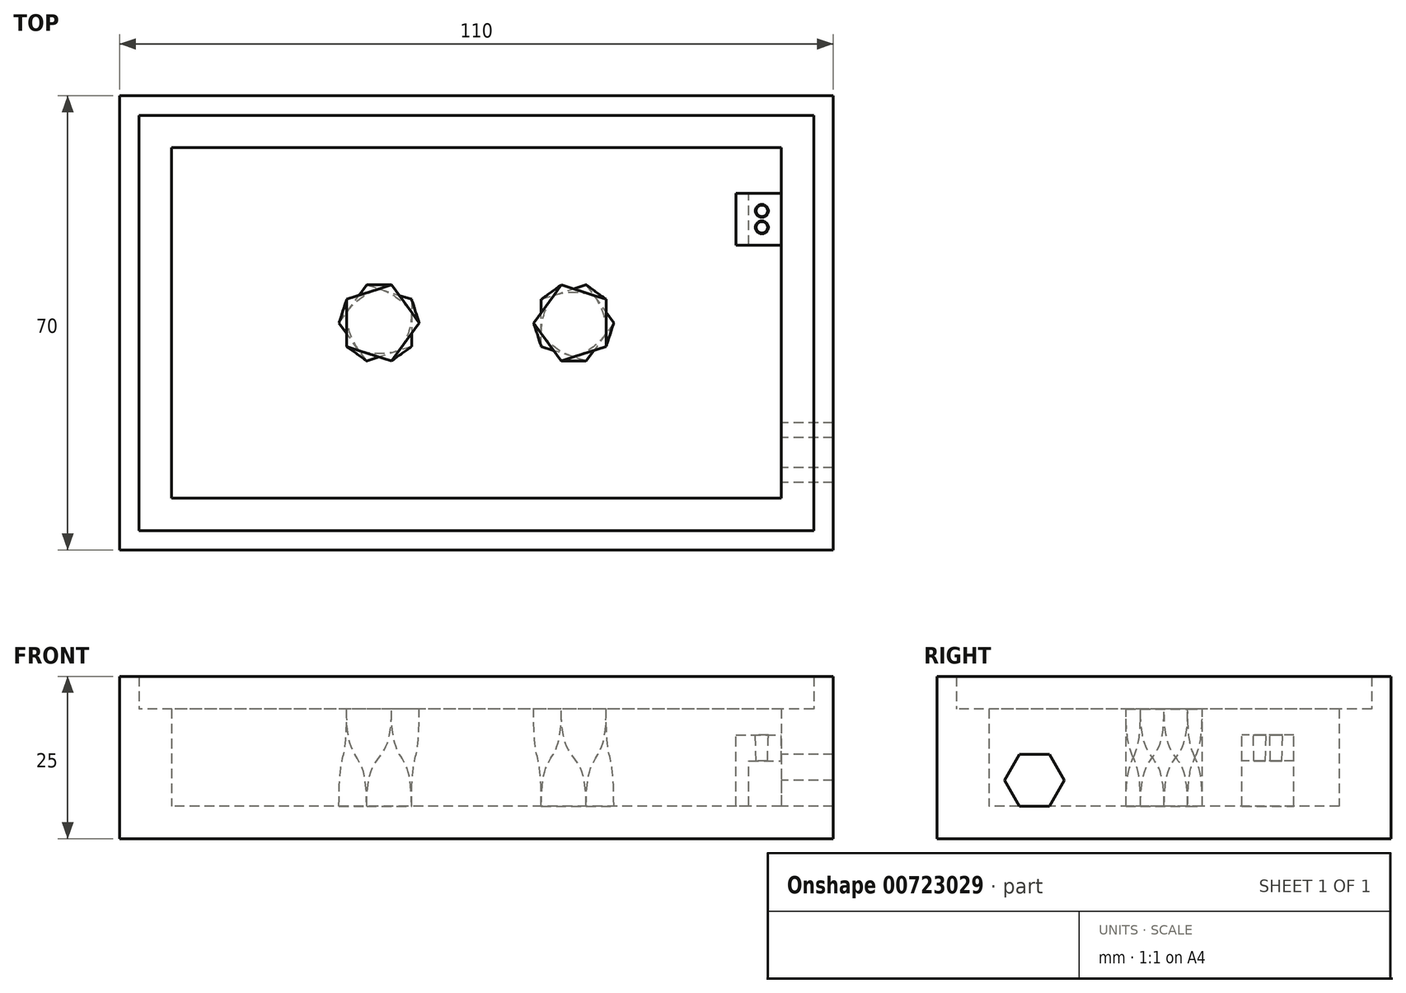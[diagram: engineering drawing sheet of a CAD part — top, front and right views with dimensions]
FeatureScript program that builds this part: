
annotation { "Feature Type Name" : "Feature", "Feature Type Description" : "" }
export const myFeature = defineFeature(function(context is Context, id is Id, definition is map)
    precondition{}
    {
        {
            var Q0;
            Q0=qCreatedBy(makeId("Top.planeOp"),FACE);
            var sketch = newSketch(context, id + "F0", { "sketchPlane" : qUnion([Q0])});
            skLineSegment(sketch, "E0.bottom", {"start": v(55, 35) * mm, "end": v(-55, 35) * mm});
            skLineSegment(sketch, "E0.top", {"start": v(55, -35) * mm, "end": v(-55, -35) * mm});
            skLineSegment(sketch, "E0.left", {"start": v(55, 35) * mm, "end": v(55, -35) * mm});
            skLineSegment(sketch, "E0.right", {"start": v(-55, 35) * mm, "end": v(-55, -35) * mm});
            skPoint(sketch, "E1", {"position": v(0, 35) * mm});
            skPoint(sketch, "E2", {"position": v(55, 0) * mm});
            skLineSegment(sketch, "E3.0", {"start": v(47, 27) * mm, "end": v(-47, 27) * mm});
            skLineSegment(sketch, "E3.1", {"start": v(47, 27) * mm, "end": v(47, -27) * mm});
            skLineSegment(sketch, "E3.2", {"start": v(47, -27) * mm, "end": v(-47, -27) * mm});
            skLineSegment(sketch, "E3.3", {"start": v(-47, 27) * mm, "end": v(-47, -27) * mm});
            skSolve(sketch);
        }
        {
            var Q0;
            Q0 = qSketchRegion(id + "F0", true);
            extrude(context, id + "F1", {"entities" : qUnion([Q0]), "depth" : 20 * mm, "offsetDistance" : 25 * mm});
        }
        {
            var Q0;
            Q0=makeQuery(id+"F1.opExtrude","CAP_FACE",FACE,{"disambiguationData":[OSD([sQuery(id+"F0.wireOp",EDGE,"E0.bottom"),sQuery(id+"F0.wireOp",EDGE,"E0.top"),sQuery(id+"F0.wireOp",EDGE,"E0.left"),sQuery(id+"F0.wireOp",EDGE,"E0.right"),sQuery(id+"F0.wireOp",EDGE,"E3.0"),sQuery(id+"F0.wireOp",EDGE,"E3.1"),sQuery(id+"F0.wireOp",EDGE,"E3.2"),sQuery(id+"F0.wireOp",EDGE,"E3.3")])],"isStart":false});
            var sketch = newSketch(context, id + "F2", { "sketchPlane" : qUnion([Q0])});
            skLineSegment(sketch, "E4.bottom", {"start": v(55, 35) * mm, "end": v(-55, 35) * mm});
            skLineSegment(sketch, "E4.top", {"start": v(55, -35) * mm, "end": v(-55, -35) * mm});
            skLineSegment(sketch, "E4.left", {"start": v(55, 35) * mm, "end": v(55, -35) * mm});
            skLineSegment(sketch, "E4.right", {"start": v(-55, 35) * mm, "end": v(-55, -35) * mm});
            skLineSegment(sketch, "E5.bottom", {"start": v(52, 32) * mm, "end": v(-52, 32) * mm});
            skLineSegment(sketch, "E5.top", {"start": v(52, -32) * mm, "end": v(-52, -32) * mm});
            skLineSegment(sketch, "E5.left", {"start": v(52, 32) * mm, "end": v(52, -32) * mm});
            skLineSegment(sketch, "E5.right", {"start": v(-52, 32) * mm, "end": v(-52, -32) * mm});
            skSolve(sketch);
        }
        {
            var Q0;
            Q0 = qSketchRegion(id + "F2", true);
            extrude(context, id + "F3", {"entities" : qUnion([Q0]), "operationType" : NewBodyOperationType.ADD, "depth" : 5 * mm, "offsetDistance" : 25 * mm});
        }
        {
            var Q0;
            Q0=makeQuery(id+"F1.opExtrude","CAP_FACE",FACE,{"disambiguationData":[OSD([sQuery(id+"F0.wireOp",EDGE,"E0.bottom"),sQuery(id+"F0.wireOp",EDGE,"E0.top"),sQuery(id+"F0.wireOp",EDGE,"E0.left"),sQuery(id+"F0.wireOp",EDGE,"E0.right"),sQuery(id+"F0.wireOp",EDGE,"E3.0"),sQuery(id+"F0.wireOp",EDGE,"E3.1"),sQuery(id+"F0.wireOp",EDGE,"E3.2"),sQuery(id+"F0.wireOp",EDGE,"E3.3")])],"isStart":true});
            var sketch = newSketch(context, id + "F4", { "sketchPlane" : qUnion([Q0])});
            skLineSegment(sketch, "E6.bottom", {"start": v(47, -27) * mm, "end": v(-47, -27) * mm});
            skLineSegment(sketch, "E6.top", {"start": v(47, 27) * mm, "end": v(-47, 27) * mm});
            skLineSegment(sketch, "E6.left", {"start": v(47, -27) * mm, "end": v(47, 27) * mm});
            skLineSegment(sketch, "E6.right", {"start": v(-47, -27) * mm, "end": v(-47, 27) * mm});
            skSolve(sketch);
        }
        {
            var Q0;
            Q0 = qSketchRegion(id + "F4", true);
            extrude(context, id + "F5", {"entities" : qUnion([Q0]), "operationType" : NewBodyOperationType.ADD, "oppositeDirection" : true, "depth" : 5 * mm, "offsetDistance" : 25 * mm});
        }
        {
            var Q0;
            Q0=makeQuery(id+"F1.opExtrude","SWEPT_FACE",FACE,{"disambiguationData":[OSD([sQuery(id+"F0.wireOp",EDGE,"E3.1")])]});
            var sketch = newSketch(context, id + "F6", { "sketchPlane" : qUnion([Q0])});
            skLineSegment(sketch, "E7.bottom", {"start": v(-20, 12) * mm, "end": v(-12, 12) * mm});
            skLineSegment(sketch, "E7.top", {"start": v(-20, 16) * mm, "end": v(-12, 16) * mm});
            skLineSegment(sketch, "E7.left", {"start": v(-20, 12) * mm, "end": v(-20, 16) * mm});
            skLineSegment(sketch, "E7.right", {"start": v(-12, 12) * mm, "end": v(-12, 16) * mm});
            skSolve(sketch);
        }
        {
            var Q0;
            Q0 = qSketchRegion(id + "F6", true);
            extrude(context, id + "F7", {"entities" : qUnion([Q0]), "operationType" : NewBodyOperationType.ADD, "depth" : 7 * mm, "offsetDistance" : 25 * mm});
        }
        {
            var Q0;
            Q0=makeQuery(id+"F7.opExtrude","SWEPT_FACE",FACE,{"disambiguationData":[OSD([sQuery(id+"F6.wireOp",EDGE,"E7.top")])]});
            var sketch = newSketch(context, id + "F8", { "sketchPlane" : qUnion([Q0])});
            skLineSegment(sketch, "E8.bottom", {"start": v(40, 20) * mm, "end": v(42, 20) * mm});
            skLineSegment(sketch, "E8.top", {"start": v(40, 12) * mm, "end": v(42, 12) * mm});
            skLineSegment(sketch, "E8.left", {"start": v(40, 20) * mm, "end": v(40, 12) * mm});
            skLineSegment(sketch, "E8.right", {"start": v(42, 20) * mm, "end": v(42, 12) * mm});
            skSolve(sketch);
        }
        {
            var Q0;
            Q0 = qSketchRegion(id + "F8", true);
            extrude(context, id + "F9", {"entities" : qUnion([Q0]), "operationType" : NewBodyOperationType.ADD, "oppositeDirection" : true, "depth" : 15 * mm, "offsetDistance" : 25 * mm});
        }
        {
            var Q0;
            Q0=makeQuery(id+"F7.opExtrude","SWEPT_FACE",FACE,{"disambiguationData":[OSD([sQuery(id+"F6.wireOp",EDGE,"E7.top")])]});
            var sketch = newSketch(context, id + "F10", { "sketchPlane" : qUnion([Q0])});
            skLineSegment(sketch, "E9.bottom", {"start": v(47, 20) * mm, "end": v(41, 20) * mm, "construction": true});
            skLineSegment(sketch, "E9.top", {"start": v(47, 12) * mm, "end": v(41, 12) * mm, "construction": true});
            skLineSegment(sketch, "E9.left", {"start": v(47, 20) * mm, "end": v(47, 12) * mm, "construction": true});
            skLineSegment(sketch, "E9.right", {"start": v(41, 20) * mm, "end": v(41, 12) * mm, "construction": true});
            skCircle(sketch, "E10", {"center": v(44, 17.27) * mm, "radius": 1 * mm});
            skCircle(sketch, "E11", {"center": v(44, 14.73) * mm, "radius": 1 * mm});
            skLineSegment(sketch, "E12", {"start": v(47, 16) * mm, "end": v(41, 16) * mm, "construction": true});
            skLineSegment(sketch, "E13", {"start": v(44, 17.27) * mm, "end": v(44, 14.73) * mm, "construction": true});
            skPoint(sketch, "E14", {"position": v(44, 16) * mm});
            skSolve(sketch);
        }
        {
            var Q0;
            Q0 = qSketchRegion(id + "F10", true);
            extrude(context, id + "F11", {"entities" : qUnion([Q0]), "operationType" : NewBodyOperationType.REMOVE, "oppositeDirection" : true, "depth" : 10 * mm, "offsetDistance" : 25 * mm, "hasDraft" : true, "draftAngle" : 1.75 * degree, "draftPullDirection" : true});
        }
        {
            var Q0;
            Q0=makeQuery(id+"F1.opExtrude","SWEPT_FACE",FACE,{"disambiguationData":[OSD([sQuery(id+"F0.wireOp",EDGE,"E3.1")])]});
            var sketch = newSketch(context, id + "F12", { "sketchPlane" : qUnion([Q0])});
            skCircle(sketch, "E15.cCircle", {"center": v(20, 9) * mm, "radius": 4 * mm, "construction": true});
            skLineSegment(sketch, "E15.0", {"start": v(15.38, 9) * mm, "end": v(17.7, 13) * mm});
            skLineSegment(sketch, "E15.1", {"start": v(17.7, 13) * mm, "end": v(22.3, 13) * mm});
            skLineSegment(sketch, "E15.2", {"start": v(22.3, 13) * mm, "end": v(24.62, 9) * mm});
            skLineSegment(sketch, "E15.3", {"start": v(24.62, 9) * mm, "end": v(22.3, 5) * mm});
            skLineSegment(sketch, "E15.4", {"start": v(22.3, 5) * mm, "end": v(17.7, 5) * mm});
            skLineSegment(sketch, "E15.5", {"start": v(17.7, 5) * mm, "end": v(15.38, 9) * mm});
            skPoint(sketch, "E15.0.midPoint", {"position": v(16.54, 11) * mm});
            skSolve(sketch);
        }
        {
            var Q0;
            Q0 = qSketchRegion(id + "F12", true);
            extrude(context, id + "F13", {"entities" : qUnion([Q0]), "operationType" : NewBodyOperationType.REMOVE, "oppositeDirection" : true, "depth" : 25 * mm, "offsetDistance" : 25 * mm});
        }
        {
            var Q0;
            Q0=makeQuery(id+"F13.boolean.opBoolean","MERGE",FACE,{"derivedFrom":[makeQuery(id+"F5.opExtrude","CAP_FACE",FACE,{"disambiguationData":[OSD([sQuery(id+"F4.wireOp",EDGE,"E6.bottom"),sQuery(id+"F4.wireOp",EDGE,"E6.top"),sQuery(id+"F4.wireOp",EDGE,"E6.left"),sQuery(id+"F4.wireOp",EDGE,"E6.right")])],"isStart":false}),makeQuery(id+"F13.opExtrude","SWEPT_FACE",FACE,{"disambiguationData":[OSD([sQuery(id+"F12.wireOp",EDGE,"E15.4")])]})]});
            var sketch = newSketch(context, id + "F14", { "sketchPlane" : qUnion([Q0])});
            skCircle(sketch, "E16.cCircle", {"center": v(-15, 0) * mm, "radius": 5 * mm, "construction": true});
            skLineSegment(sketch, "E16.0", {"start": v(-10, 3.63) * mm, "end": v(-10, -3.63) * mm});
            skLineSegment(sketch, "E16.1", {"start": v(-10, -3.63) * mm, "end": v(-16.9, -5.88) * mm});
            skLineSegment(sketch, "E16.2", {"start": v(-16.9, -5.88) * mm, "end": v(-21.18, 0) * mm});
            skLineSegment(sketch, "E16.3", {"start": v(-21.18, 0) * mm, "end": v(-16.9, 5.88) * mm});
            skLineSegment(sketch, "E16.4", {"start": v(-16.9, 5.88) * mm, "end": v(-10, 3.63) * mm});
            skPoint(sketch, "E16.0.midPoint", {"position": v(-10, 0) * mm});
            skSolve(sketch);
        }
        {
            var Q0;
            Q0=makeQuery(id+"F14.imprint","IMPRINT",FACE,{"disambiguationData":[TD([[makeQuery(id+"F14.imprint","IMPRINT",EDGE,{"derivedFrom":sQuery(id+"F14.wireOp",EDGE,"E16.0")}),1.0]])]});
            cPlane(context, id + "F15", {"entities" : qUnion([Q0]), "cplaneType" : CPlaneType.OFFSET, "offset" : 15 * mm, "width" : 150 * mm, "height" : 150 * mm});
        }
        {
            var Q0;
            Q0=qCreatedBy(id+"F15.planeOp",FACE);
            var sketch = newSketch(context, id + "F16", { "sketchPlane" : qUnion([Q0])});
            skCircle(sketch, "E17.cCircle", {"center": v(-15, 0) * mm, "radius": 5 * mm, "construction": true});
            skLineSegment(sketch, "E17.0", {"start": v(-8.82, 0) * mm, "end": v(-13.1, -5.88) * mm});
            skLineSegment(sketch, "E17.1", {"start": v(-13.1, -5.88) * mm, "end": v(-20, -3.63) * mm});
            skLineSegment(sketch, "E17.2", {"start": v(-20, -3.63) * mm, "end": v(-20, 3.63) * mm});
            skLineSegment(sketch, "E17.3", {"start": v(-20, 3.63) * mm, "end": v(-13.1, 5.88) * mm});
            skLineSegment(sketch, "E17.4", {"start": v(-13.1, 5.88) * mm, "end": v(-8.82, 0) * mm});
            skPoint(sketch, "E18.0.midPoint", {"position": v(10, 0) * mm});
            skSolve(sketch);
        }
        {
            var Q1;
            Q1 = qSketchRegion(id + "F14", true);
            var Q2;
            Q2 = qSketchRegion(id + "F16", true);
            loft(context, id + "F17", {"operationType" : NewBodyOperationType.ADD, "startCondition" : LoftEndDerivativeType.NORMAL_TO_PROFILE, "startMagnitude" : 2, "endCondition" : LoftEndDerivativeType.NORMAL_TO_PROFILE, "endMagnitude" : 2, "sheetProfilesArray" : [{ "sheetProfileEntities" : qUnion([Q1]) }, { "sheetProfileEntities" : qUnion([Q2]) }]});
        }
        {
            var Q0;
            Q0=makeQuery(id+"F13.boolean.opBoolean","MERGE",FACE,{"derivedFrom":[makeQuery(id+"F5.opExtrude","CAP_FACE",FACE,{"disambiguationData":[OSD([sQuery(id+"F4.wireOp",EDGE,"E6.bottom"),sQuery(id+"F4.wireOp",EDGE,"E6.top"),sQuery(id+"F4.wireOp",EDGE,"E6.left"),sQuery(id+"F4.wireOp",EDGE,"E6.right")])],"isStart":false}),makeQuery(id+"F13.opExtrude","SWEPT_FACE",FACE,{"disambiguationData":[OSD([sQuery(id+"F12.wireOp",EDGE,"E15.4")])]})]});
            var sketch = newSketch(context, id + "F18", { "sketchPlane" : qUnion([Q0])});
            skCircle(sketch, "E19.cCircle", {"center": v(15, 0) * mm, "radius": 5 * mm, "construction": true});
            skLineSegment(sketch, "E19.0", {"start": v(16.9, 5.88) * mm, "end": v(21.18, 0) * mm});
            skLineSegment(sketch, "E19.1", {"start": v(21.18, 0) * mm, "end": v(16.9, -5.88) * mm});
            skLineSegment(sketch, "E19.2", {"start": v(16.9, -5.88) * mm, "end": v(10, -3.63) * mm});
            skLineSegment(sketch, "E19.3", {"start": v(10, -3.63) * mm, "end": v(10, 3.63) * mm});
            skLineSegment(sketch, "E19.4", {"start": v(10, 3.63) * mm, "end": v(16.9, 5.88) * mm});
            skPoint(sketch, "E19.0.midPoint", {"position": v(19.05, 2.94) * mm});
            skSolve(sketch);
        }
        {
            var Q0;
            Q0=qCreatedBy(id+"F15.planeOp",FACE);
            var sketch = newSketch(context, id + "F19", { "sketchPlane" : qUnion([Q0])});
            skCircle(sketch, "E20.cCircle", {"center": v(15, 0) * mm, "radius": 5 * mm, "construction": true});
            skLineSegment(sketch, "E20.0", {"start": v(8.82, 0) * mm, "end": v(13.1, 5.88) * mm});
            skLineSegment(sketch, "E20.1", {"start": v(13.1, 5.88) * mm, "end": v(20, 3.63) * mm});
            skLineSegment(sketch, "E20.2", {"start": v(20, 3.63) * mm, "end": v(20, -3.63) * mm});
            skLineSegment(sketch, "E20.3", {"start": v(20, -3.63) * mm, "end": v(13.1, -5.88) * mm});
            skLineSegment(sketch, "E20.4", {"start": v(13.1, -5.88) * mm, "end": v(8.82, 0) * mm});
            skPoint(sketch, "E20.0.midPoint", {"position": v(10.95, 2.94) * mm});
            skSolve(sketch);
        }
        {
            var Q1;
            Q1 = qSketchRegion(id + "F18", true);
            var Q2;
            Q2 = qSketchRegion(id + "F19", true);
            loft(context, id + "F20", {"operationType" : NewBodyOperationType.ADD, "startCondition" : LoftEndDerivativeType.NORMAL_TO_PROFILE, "startMagnitude" : 2, "endCondition" : LoftEndDerivativeType.NORMAL_TO_PROFILE, "endMagnitude" : 2, "sheetProfilesArray" : [{ "sheetProfileEntities" : qUnion([Q1]) }, { "sheetProfileEntities" : qUnion([Q2]) }]});
        }
    });
